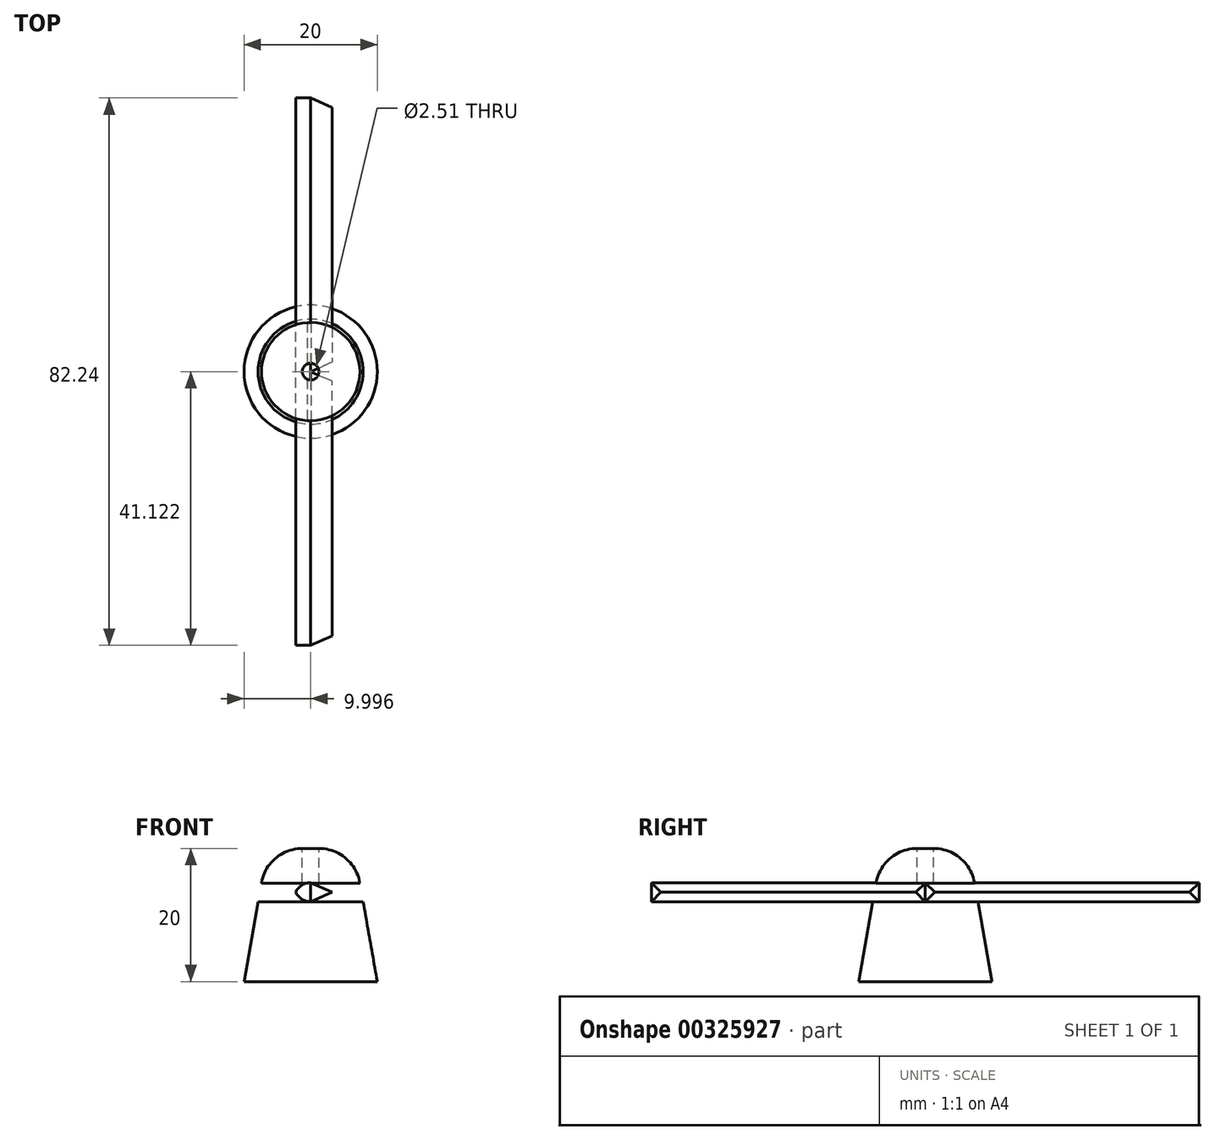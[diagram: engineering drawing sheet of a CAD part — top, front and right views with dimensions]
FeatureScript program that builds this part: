
annotation { "Feature Type Name" : "Feature", "Feature Type Description" : "" }
export const myFeature = defineFeature(function(context is Context, id is Id, definition is map)
    precondition{}
    {
        {
            var Q0;
            Q0=qCreatedBy(makeId("Top.planeOp"),FACE);
            var sketch = newSketch(context, id + "F0", { "sketchPlane" : qUnion([Q0])});
            skCircle(sketch, "E0", {"center": v(43.7, 48.55) * mm, "radius": 10 * mm});
            skCircle(sketch, "E1", {"center": v(43.7, 48.55) * mm, "radius": 1 * mm});
            skSolve(sketch);
        }
        {
            var Q0;
            Q0=makeQuery(id+"F0.imprint","IMPRINT",FACE,{"disambiguationData":[TD([[makeQuery(id+"F0.imprint","IMPRINT",EDGE,{"derivedFrom":sQuery(id+"F0.wireOp",EDGE,"E1")}),1.0]])]});
            var Q1;
            Q1=makeQuery(id+"F0.imprint","IMPRINT",FACE,{"disambiguationData":[TD([[makeQuery(id+"F0.imprint","IMPRINT",EDGE,{"derivedFrom":sQuery(id+"F0.wireOp",EDGE,"E0")}),1.0]])]});
            extrude(context, id + "F1", {"entities" : qUnion([Q0, Q1]), "depth" : 20 * mm, "hasDraft" : true, "draftAngle" : 10 * degree, "draftPullDirection" : true});
        }
        {
            var Q0;
            Q0=makeQuery(id+"F1.opExtrude","CAP_EDGE",EDGE,{"disambiguationData":[OSD([sQuery(id+"F0.wireOp",EDGE,"E0")])],"isStart":false});
            fillet(context, id + "F2", {"entities" : qUnion([Q0]), "radius" : 6.22 * mm, "tangentPropagation" : true, "allowEdgeOverflow" : false});
        }
        {
            var Q0;
            Q0=makeQuery(id+"F1.opExtrude","CAP_FACE",FACE,{"disambiguationData":[OSD([sQuery(id+"F0.wireOp",EDGE,"E0")])],"isStart":false});
            extrude(context, id + "F3", {"entities" : qUnion([Q0]), "operationType" : NewBodyOperationType.REMOVE, "oppositeDirection" : true, "depth" : 25 * mm});
        }
        {
            var Q0;
            Q0=makeQuery(id+"F1.opExtrude","CAP_FACE",FACE,{"disambiguationData":[OSD([sQuery(id+"F0.wireOp",EDGE,"E0")])],"isStart":true});
            var Q1;
            Q1=makeQuery(id+"F2.opFillet","BLEND_FACE",FACE,{"disambiguationData":[OSD([sQuery(id+"F0.wireOp",EDGE,"E0")])]});
            extrude(context, id + "F4", {"entities" : qUnion([Q0]), "operationType" : NewBodyOperationType.REMOVE, "oppositeDirection" : true, "endBoundEntityFace" : qUnion([Q1]), "depth" : 14.8 * mm});
        }
        {
            var Q0;
            Q0=makeQuery(id+"F0.imprint","IMPRINT",FACE,{"disambiguationData":[TD([[makeQuery(id+"F0.imprint","IMPRINT",EDGE,{"derivedFrom":sQuery(id+"F0.wireOp",EDGE,"E0")}),1.0]])]});
            var Q1;
            Q1=makeQuery(id+"F0.imprint","IMPRINT",FACE,{"disambiguationData":[TD([[makeQuery(id+"F0.imprint","IMPRINT",EDGE,{"derivedFrom":sQuery(id+"F0.wireOp",EDGE,"E1")}),1.0]])]});
            extrude(context, id + "F5", {"entities" : qUnion([Q0, Q1]), "depth" : 12 * mm, "hasDraft" : true, "draftAngle" : 10 * degree, "draftPullDirection" : true});
        }
        {
            var Q0;
            Q0=sQuery(id+"F0.wireOp",VERTEX,"E0.center");
            var Q1;
            Q1=qCreatedBy(makeId("Right.planeOp"),FACE);
            cPlane(context, id + "F6", {"entities" : qUnion([Q0, Q1]), "cplaneType" : CPlaneType.PLANE_POINT, "offset" : 25 * mm, "width" : 150 * mm, "height" : 150 * mm});
        }
        {
            var Q0;
            Q0=qCreatedBy(id+"F6.planeOp",FACE);
            var sketch = newSketch(context, id + "F7", { "sketchPlane" : qUnion([Q0])});
            skLineSegment(sketch, "E2.bottom", {"start": v(48.55, 14.86) * mm, "end": v(7.43, 14.86) * mm});
            skLineSegment(sketch, "E2.top", {"start": v(48.55, 12) * mm, "end": v(7.43, 12) * mm});
            skLineSegment(sketch, "E2.left", {"start": v(48.55, 14.86) * mm, "end": v(48.55, 12) * mm});
            skLineSegment(sketch, "E2.right", {"start": v(7.43, 14.86) * mm, "end": v(7.43, 12) * mm});
            skPoint(sketch, "E3", {"position": v(70.17, 12) * mm});
            skPoint(sketch, "E4", {"position": v(70.17, 14.86) * mm});
            skSolve(sketch);
        }
        {
            var Q0;
            Q0=makeQuery(id+"F7.imprint","IMPRINT",FACE,{"disambiguationData":[TD([[makeQuery(id+"F7.imprint","IMPRINT",EDGE,{"derivedFrom":sQuery(id+"F7.wireOp",EDGE,"E2.bottom")}),1.0]])]});
            extrude(context, id + "F8", {"entities" : qUnion([Q0]), "depth" : 4 * mm, "hasDraft" : true, "draftAngle" : 24 * degree, "draftPullDirection" : true, "hasSecondDirection" : true, "secondDirectionOppositeDirection" : true, "secondDirectionDepth" : 2.5 * mm});
        }
        {
            var Q0;
            Q0=makeQuery(id+"F8.opExtrude","CAP_EDGE",EDGE,{"disambiguationData":[OSD([sQuery(id+"F7.wireOp",EDGE,"E2.top")])],"isStart":true});
            var Q1;
            Q1=makeQuery(id+"F8.opExtrude","CAP_EDGE",EDGE,{"disambiguationData":[OSD([sQuery(id+"F7.wireOp",EDGE,"E2.bottom")])],"isStart":true});
            fillet(context, id + "F9", {"entities" : qUnion([Q0, Q1]), "radius" : 2.5 * mm, "tangentPropagation" : true, "allowEdgeOverflow" : false});
        }
        {
            var Q0;
            Q0=makeQuery(id+"F8.*.split.splitOp","SPLIT",BODY,{"derivedFrom":makeQuery(id+"F8.opExtrude","SWEPT_BODY",BODY,{"disambiguationData":[OSD([sQuery(id+"F7.wireOp",EDGE,"E2.bottom"),sQuery(id+"F7.wireOp",EDGE,"E2.top"),sQuery(id+"F7.wireOp",EDGE,"E2.left"),sQuery(id+"F7.wireOp",EDGE,"E2.right")])]})});
            var Q1;
            Q1=makeQuery(id+"F8.*.split.splitOp","SPLIT",FACE,{"derivedFrom":makeQuery(id+"F8.opExtrude","SWEPT_FACE",FACE,{"disambiguationData":[OSD([sQuery(id+"F7.wireOp",EDGE,"E2.left")])]}),"isFromBackBody":true});
            mirror(context, id + "F10", {"operationType" : NewBodyOperationType.ADD, "entities" : qUnion([Q0]), "mirrorPlane" : qUnion([Q1])});
        }
    });
